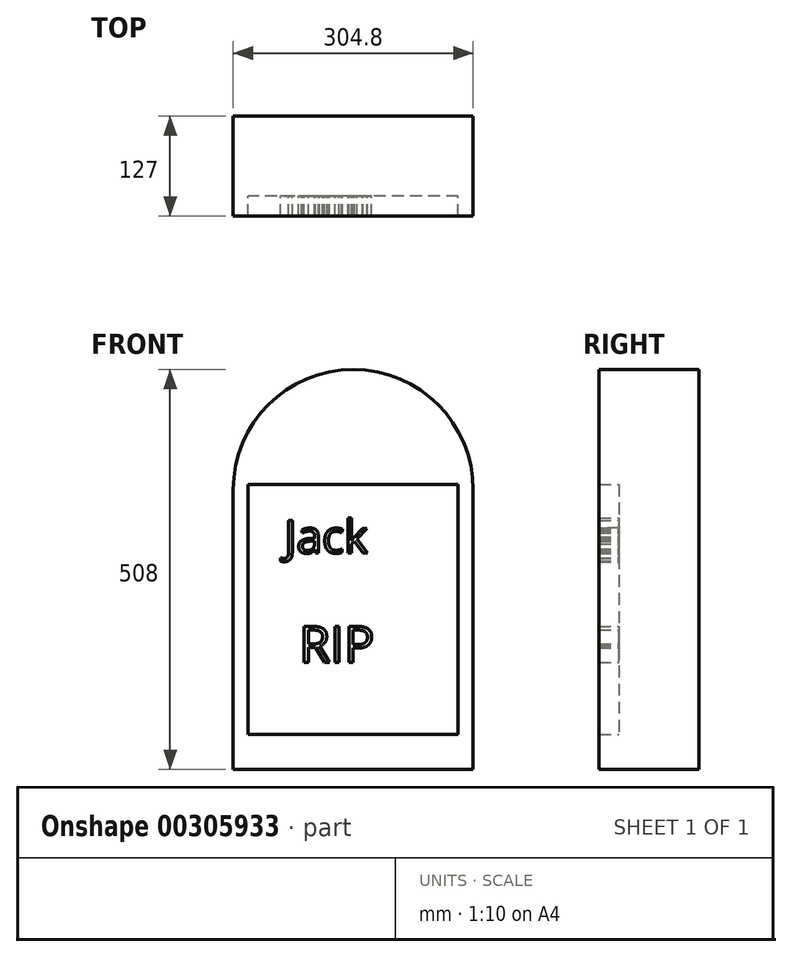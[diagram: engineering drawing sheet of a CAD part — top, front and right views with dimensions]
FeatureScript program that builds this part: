
annotation { "Feature Type Name" : "Feature", "Feature Type Description" : "" }
export const myFeature = defineFeature(function(context is Context, id is Id, definition is map)
    precondition{}
    {
        {
            var Q0;
            Q0=qCreatedBy(makeId("Front.planeOp"),FACE);
            var sketch = newSketch(context, id + "F0", { "sketchPlane" : qUnion([Q0])});
            skLineSegment(sketch, "E0.top", {"start": v(-180.02, -72.98) * mm, "end": v(124.78, -72.98) * mm});
            skLineSegment(sketch, "E0.left", {"start": v(-180.02, 282.62) * mm, "end": v(-180.02, -72.98) * mm});
            skLineSegment(sketch, "E0.right", {"start": v(124.78, 282.62) * mm, "end": v(124.78, -72.98) * mm});
            skArc(sketch, "E1", {"start": v(124.78, 282.62) * mm, "mid": v(-27.62, 435.02) * mm, "end": v(-180.02, 282.62) * mm});
            skSolve(sketch);
        }
        {
            var Q0;
            Q0=makeQuery(id+"F0.imprint","IMPRINT",FACE,{"disambiguationData":[TD([[makeQuery(id+"F0.imprint","IMPRINT",EDGE,{"derivedFrom":sQuery(id+"F0.wireOp",EDGE,"E0.top")}),1.0]])]});
            extrude(context, id + "F1", {"entities" : qUnion([Q0]), "depth" : 101.6 * mm});
        }
        {
            var Q0;
            Q0=makeQuery(id+"F1.opExtrude","CAP_FACE",FACE,{"disambiguationData":[OSD([sQuery(id+"F0.wireOp",EDGE,"E0.top"),sQuery(id+"F0.wireOp",EDGE,"E0.left"),sQuery(id+"F0.wireOp",EDGE,"E0.right"),sQuery(id+"F0.wireOp",EDGE,"E1")])],"isStart":false});
            var sketch = newSketch(context, id + "F2", { "sketchPlane" : qUnion([Q0])});
            skLineSegment(sketch, "E2.bottom", {"start": v(99.25, 282.62) * mm, "end": v(-154.75, 282.62) * mm});
            skLineSegment(sketch, "E2.top", {"start": v(99.25, -22.18) * mm, "end": v(-154.75, -22.18) * mm});
            skLineSegment(sketch, "E2.left", {"start": v(99.25, 282.62) * mm, "end": v(99.25, -22.18) * mm});
            skLineSegment(sketch, "E2.right", {"start": v(-154.75, 282.62) * mm, "end": v(-154.75, -22.18) * mm});
            skLineSegment(sketch, "E3.0", {"start": v(105.6, 288.97) * mm, "end": v(-161.1, 288.97) * mm});
            skLineSegment(sketch, "E3.1", {"start": v(105.6, 288.97) * mm, "end": v(105.6, -28.53) * mm});
            skLineSegment(sketch, "E3.2", {"start": v(105.6, -28.53) * mm, "end": v(-161.1, -28.53) * mm});
            skLineSegment(sketch, "E3.3", {"start": v(-161.1, 288.97) * mm, "end": v(-161.1, -28.53) * mm});
            skSolve(sketch);
        }
        {
            var Q0;
            Q0=makeQuery(id+"F2.imprint","IMPRINT",FACE,{"disambiguationData":[TD([[makeQuery(id+"F2.imprint","IMPRINT",EDGE,{"derivedFrom":sQuery(id+"F2.wireOp",EDGE,"E3.0")}),-1.0]])]});
            extrude(context, id + "F3", {"entities" : qUnion([Q0]), "operationType" : NewBodyOperationType.ADD, "depth" : 25.4 * mm});
        }
        {
            var Q0;
            Q0=makeQuery(id+"F1.opExtrude","CAP_FACE",FACE,{"disambiguationData":[OSD([sQuery(id+"F0.wireOp",EDGE,"E0.top"),sQuery(id+"F0.wireOp",EDGE,"E0.left"),sQuery(id+"F0.wireOp",EDGE,"E0.right"),sQuery(id+"F0.wireOp",EDGE,"E1")])],"isStart":false});
            var sketch = newSketch(context, id + "F4", { "sketchPlane" : qUnion([Q0])});
            skText(sketch, "E4", { "text": "Jack", "fontName": "OpenSans-Regular.ttf"});
            skText(sketch, "E5", { "text": "RIP\n", "fontName": "OpenSans-Regular.ttf"});
            const initialGuessF4  = {"E4": [-0.11532, 0.20185, 1, 0, 0.0421], "E5": [-0.09623, 0.0632, 1, 0, 0.0458]};
            skSetInitialGuess(sketch, initialGuessF4);
            skSolve(sketch);
        }
        {
            var Q0;
            Q0 = qSketchRegion(id + "F4", true);
            extrude(context, id + "F5", {"entities" : qUnion([Q0]), "operationType" : NewBodyOperationType.ADD, "depth" : 25.4 * mm});
        }
    });
